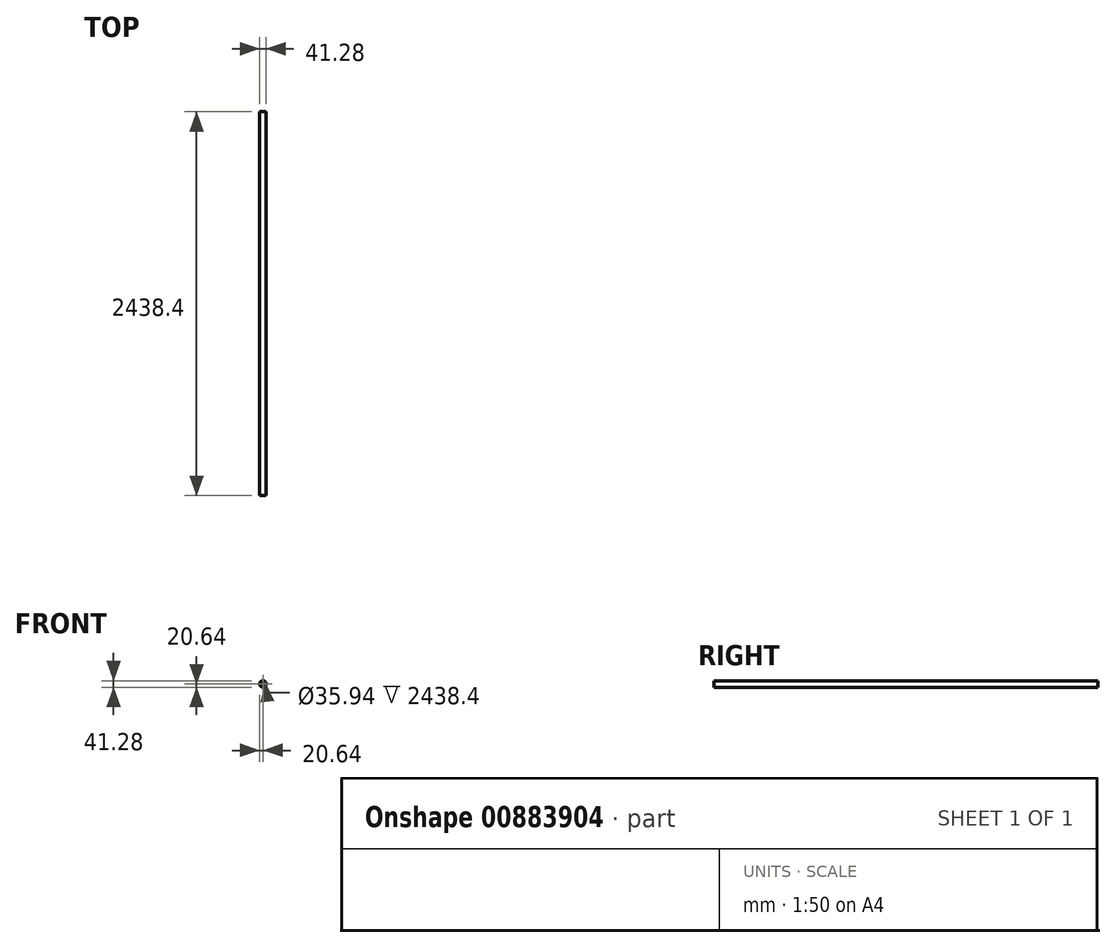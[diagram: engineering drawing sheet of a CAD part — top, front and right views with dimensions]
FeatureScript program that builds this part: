
annotation { "Feature Type Name" : "Feature", "Feature Type Description" : "" }
export const myFeature = defineFeature(function(context is Context, id is Id, definition is map)
    precondition{}
    {
        {
            var Q0;
            Q0=qCreatedBy(makeId("Front.planeOp"),FACE);
            var sketch = newSketch(context, id + "F0", { "sketchPlane" : qUnion([Q0])});
            skCircle(sketch, "E0", {"center": v(0, 0) * mm, "radius": 20.64 * mm});
            skCircle(sketch, "E1.0", {"center": v(0, 0) * mm, "radius": 17.97 * mm});
            skSolve(sketch);
        }
        {
            var Q0;
            Q0 = qSketchRegion(id + "F0", true);
            extrude(context, id + "F1", {"entities" : qUnion([Q0]), "oppositeDirection" : true, "depth" : 2438.4 * mm, "offsetDistance" : 25.4 * mm});
        }
    });
